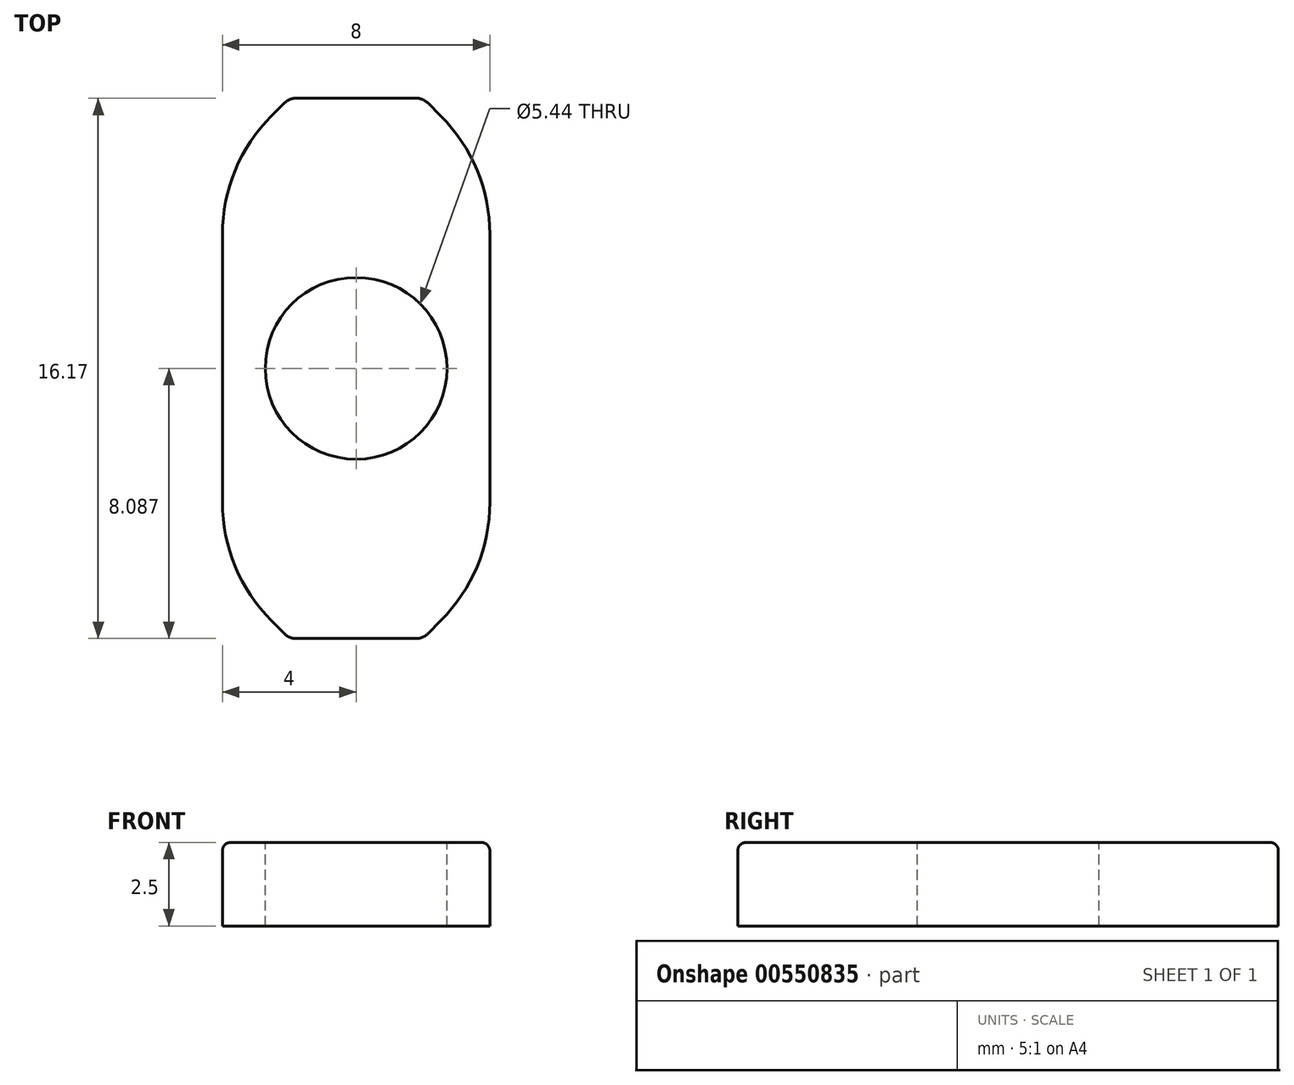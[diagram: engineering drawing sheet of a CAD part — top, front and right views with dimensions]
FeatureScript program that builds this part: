
annotation { "Feature Type Name" : "Feature", "Feature Type Description" : "" }
export const myFeature = defineFeature(function(context is Context, id is Id, definition is map)
    precondition{}
    {
        {
            var Q0;
            Q0=qCreatedBy(makeId("Top.planeOp"),FACE);
            var sketch = newSketch(context, id + "F0", { "sketchPlane" : qUnion([Q0])});
            skLineSegment(sketch, "E0.bottom", {"start": v(-52.87, 0) * mm, "end": v(-44.87, 0) * mm});
            skLineSegment(sketch, "E0.top", {"start": v(-52.87, 16.17) * mm, "end": v(-44.87, 16.17) * mm});
            skLineSegment(sketch, "E0.left", {"start": v(-52.87, 0) * mm, "end": v(-52.87, 16.17) * mm});
            skLineSegment(sketch, "E0.right", {"start": v(-44.87, 0) * mm, "end": v(-44.87, 16.17) * mm});
            skSolve(sketch);
        }
        {
            var Q0;
            Q0=makeQuery(id+"F0.imprint","IMPRINT",FACE,{"disambiguationData":[TD([[makeQuery(id+"F0.imprint","IMPRINT",EDGE,{"derivedFrom":sQuery(id+"F0.wireOp",EDGE,"E0.bottom")}),1.0]])]});
            extrude(context, id + "F1", {"entities" : qUnion([Q0]), "depth" : 2.5 * mm, "offsetDistance" : 25 * mm});
        }
        {
            var Q0;
            Q0=makeQuery(id+"F1.opExtrude","SWEPT_EDGE",EDGE,{"disambiguationData":[OSD([sQuery(id+"F0.wireOp",EDGE,"E0.bottom"),sQuery(id+"F0.wireOp",EDGE,"E0.right")])]});
            var Q1;
            Q1=makeQuery(id+"F1.opExtrude","SWEPT_EDGE",EDGE,{"disambiguationData":[OSD([sQuery(id+"F0.wireOp",EDGE,"E0.bottom"),sQuery(id+"F0.wireOp",EDGE,"E0.left")])]});
            var Q2;
            Q2=makeQuery(id+"F1.opExtrude","SWEPT_EDGE",EDGE,{"disambiguationData":[OSD([sQuery(id+"F0.wireOp",EDGE,"E0.top"),sQuery(id+"F0.wireOp",EDGE,"E0.right")])]});
            var Q3;
            Q3=makeQuery(id+"F1.opExtrude","SWEPT_EDGE",EDGE,{"disambiguationData":[OSD([sQuery(id+"F0.wireOp",EDGE,"E0.top"),sQuery(id+"F0.wireOp",EDGE,"E0.left")])]});
            chamfer(context, id + "F2", {"entities" : qUnion([Q0, Q1, Q2, Q3]), "width" : 2 * mm, "tangentPropagation" : true});
        }
        {
            var Q0;
            {var subQ0=sQuery(id+"F0.wireOp",EDGE,"E0.left");Q0=makeQuery(id+"F2.opChamfer","BLEND_EDGE",EDGE,{"blendedFrom":[makeQuery(id+"F1.opExtrude","SWEPT_EDGE",EDGE,{"disambiguationData":[OSD([sQuery(id+"F0.wireOp",EDGE,"E0.top"),subQ0])]}),makeQuery(id+"F1.opExtrude","SWEPT_FACE",FACE,{"disambiguationData":[OSD([subQ0])]})],"blendedInto":[makeQuery(id+"F1.opExtrude","SWEPT_FACE",FACE,{"disambiguationData":[OSD([subQ0])]})]});}
            var Q1;
            {var subQ0=sQuery(id+"F0.wireOp",EDGE,"E0.left");Q1=makeQuery(id+"F2.opChamfer","BLEND_EDGE",EDGE,{"blendedFrom":[makeQuery(id+"F1.opExtrude","SWEPT_EDGE",EDGE,{"disambiguationData":[OSD([sQuery(id+"F0.wireOp",EDGE,"E0.bottom"),subQ0])]}),makeQuery(id+"F1.opExtrude","SWEPT_FACE",FACE,{"disambiguationData":[OSD([subQ0])]})],"blendedInto":[makeQuery(id+"F1.opExtrude","SWEPT_FACE",FACE,{"disambiguationData":[OSD([subQ0])]})]});}
            var Q2;
            {var subQ0=sQuery(id+"F0.wireOp",EDGE,"E0.right");Q2=makeQuery(id+"F2.opChamfer","BLEND_EDGE",EDGE,{"blendedFrom":[makeQuery(id+"F1.opExtrude","SWEPT_EDGE",EDGE,{"disambiguationData":[OSD([sQuery(id+"F0.wireOp",EDGE,"E0.bottom"),subQ0])]}),makeQuery(id+"F1.opExtrude","SWEPT_FACE",FACE,{"disambiguationData":[OSD([subQ0])]})],"blendedInto":[makeQuery(id+"F1.opExtrude","SWEPT_FACE",FACE,{"disambiguationData":[OSD([subQ0])]})]});}
            var Q3;
            {var subQ0=sQuery(id+"F0.wireOp",EDGE,"E0.right");Q3=makeQuery(id+"F2.opChamfer","BLEND_EDGE",EDGE,{"blendedFrom":[makeQuery(id+"F1.opExtrude","SWEPT_EDGE",EDGE,{"disambiguationData":[OSD([sQuery(id+"F0.wireOp",EDGE,"E0.top"),subQ0])]}),makeQuery(id+"F1.opExtrude","SWEPT_FACE",FACE,{"disambiguationData":[OSD([subQ0])]})],"blendedInto":[makeQuery(id+"F1.opExtrude","SWEPT_FACE",FACE,{"disambiguationData":[OSD([subQ0])]})]});}
            fillet(context, id + "F3", {"entities" : qUnion([Q0, Q1, Q2, Q3]), "radius" : 5 * mm, "tangentPropagation" : true, "allowEdgeOverflow" : false});
        }
        {
            var Q0;
            {var subQ0=sQuery(id+"F0.wireOp",EDGE,"E0.top");Q0=makeQuery(id+"F2.opChamfer","BLEND_EDGE",EDGE,{"blendedFrom":[makeQuery(id+"F1.opExtrude","SWEPT_EDGE",EDGE,{"disambiguationData":[OSD([subQ0,sQuery(id+"F0.wireOp",EDGE,"E0.left")])]}),makeQuery(id+"F1.opExtrude","SWEPT_FACE",FACE,{"disambiguationData":[OSD([subQ0])]})],"blendedInto":[makeQuery(id+"F1.opExtrude","SWEPT_FACE",FACE,{"disambiguationData":[OSD([subQ0])]})]});}
            var Q1;
            {var subQ0=sQuery(id+"F0.wireOp",EDGE,"E0.top");Q1=makeQuery(id+"F2.opChamfer","BLEND_EDGE",EDGE,{"blendedFrom":[makeQuery(id+"F1.opExtrude","SWEPT_EDGE",EDGE,{"disambiguationData":[OSD([subQ0,sQuery(id+"F0.wireOp",EDGE,"E0.right")])]}),makeQuery(id+"F1.opExtrude","SWEPT_FACE",FACE,{"disambiguationData":[OSD([subQ0])]})],"blendedInto":[makeQuery(id+"F1.opExtrude","SWEPT_FACE",FACE,{"disambiguationData":[OSD([subQ0])]})]});}
            var Q2;
            {var subQ0=sQuery(id+"F0.wireOp",EDGE,"E0.bottom");Q2=makeQuery(id+"F2.opChamfer","BLEND_EDGE",EDGE,{"blendedFrom":[makeQuery(id+"F1.opExtrude","SWEPT_EDGE",EDGE,{"disambiguationData":[OSD([subQ0,sQuery(id+"F0.wireOp",EDGE,"E0.right")])]}),makeQuery(id+"F1.opExtrude","SWEPT_FACE",FACE,{"disambiguationData":[OSD([subQ0])]})],"blendedInto":[makeQuery(id+"F1.opExtrude","SWEPT_FACE",FACE,{"disambiguationData":[OSD([subQ0])]})]});}
            var Q3;
            {var subQ0=sQuery(id+"F0.wireOp",EDGE,"E0.bottom");Q3=makeQuery(id+"F2.opChamfer","BLEND_EDGE",EDGE,{"blendedFrom":[makeQuery(id+"F1.opExtrude","SWEPT_EDGE",EDGE,{"disambiguationData":[OSD([subQ0,sQuery(id+"F0.wireOp",EDGE,"E0.left")])]}),makeQuery(id+"F1.opExtrude","SWEPT_FACE",FACE,{"disambiguationData":[OSD([subQ0])]})],"blendedInto":[makeQuery(id+"F1.opExtrude","SWEPT_FACE",FACE,{"disambiguationData":[OSD([subQ0])]})]});}
            fillet(context, id + "F4", {"entities" : qUnion([Q0, Q1, Q2, Q3]), "radius" : .5 * mm, "tangentPropagation" : true, "allowEdgeOverflow" : false});
        }
        {
            var Q0;
            Q0=makeQuery(id+"F1.opExtrude","CAP_FACE",FACE,{"disambiguationData":[OSD([sQuery(id+"F0.wireOp",EDGE,"E0.bottom"),sQuery(id+"F0.wireOp",EDGE,"E0.top"),sQuery(id+"F0.wireOp",EDGE,"E0.left"),sQuery(id+"F0.wireOp",EDGE,"E0.right")])],"isStart":false});
            var sketch = newSketch(context, id + "F5", { "sketchPlane" : qUnion([Q0])});
            skCircle(sketch, "E1", {"center": v(-48.87, 8.09) * mm, "radius": 2.72 * mm});
            skPoint(sketch, "E1.centerSnap0", {"position": v(-48.87, 16.17) * mm});
            skPoint(sketch, "E1.centerSnap1", {"position": v(-52.87, 8.09) * mm});
            skSolve(sketch);
        }
        {
            var Q0;
            Q0 = qSketchRegion(id + "F5", true);
            extrude(context, id + "F6", {"entities" : qUnion([Q0]), "operationType" : NewBodyOperationType.REMOVE, "oppositeDirection" : true, "depth" : 25 * mm, "offsetDistance" : 25 * mm});
        }
        {
            var Q0;
            Q0=makeQuery(id+"F6.boolean.opBoolean","COPY",EDGE,{"derivedFrom":makeQuery(id+"F6.opExtrude","CAP_EDGE",EDGE,{"disambiguationData":[OSD([sQuery(id+"F5.wireOp",EDGE,"E1")])],"isStart":true})});
            var Q1;
            Q1=makeQuery(id+"F1.opExtrude","CAP_EDGE",EDGE,{"disambiguationData":[OSD([sQuery(id+"F0.wireOp",EDGE,"E0.left")])],"isStart":false});
            fillet(context, id + "F7", {"entities" : qUnion([Q0, Q1]), "radius" : .25 * mm, "tangentPropagation" : true, "allowEdgeOverflow" : false});
        }
    });
